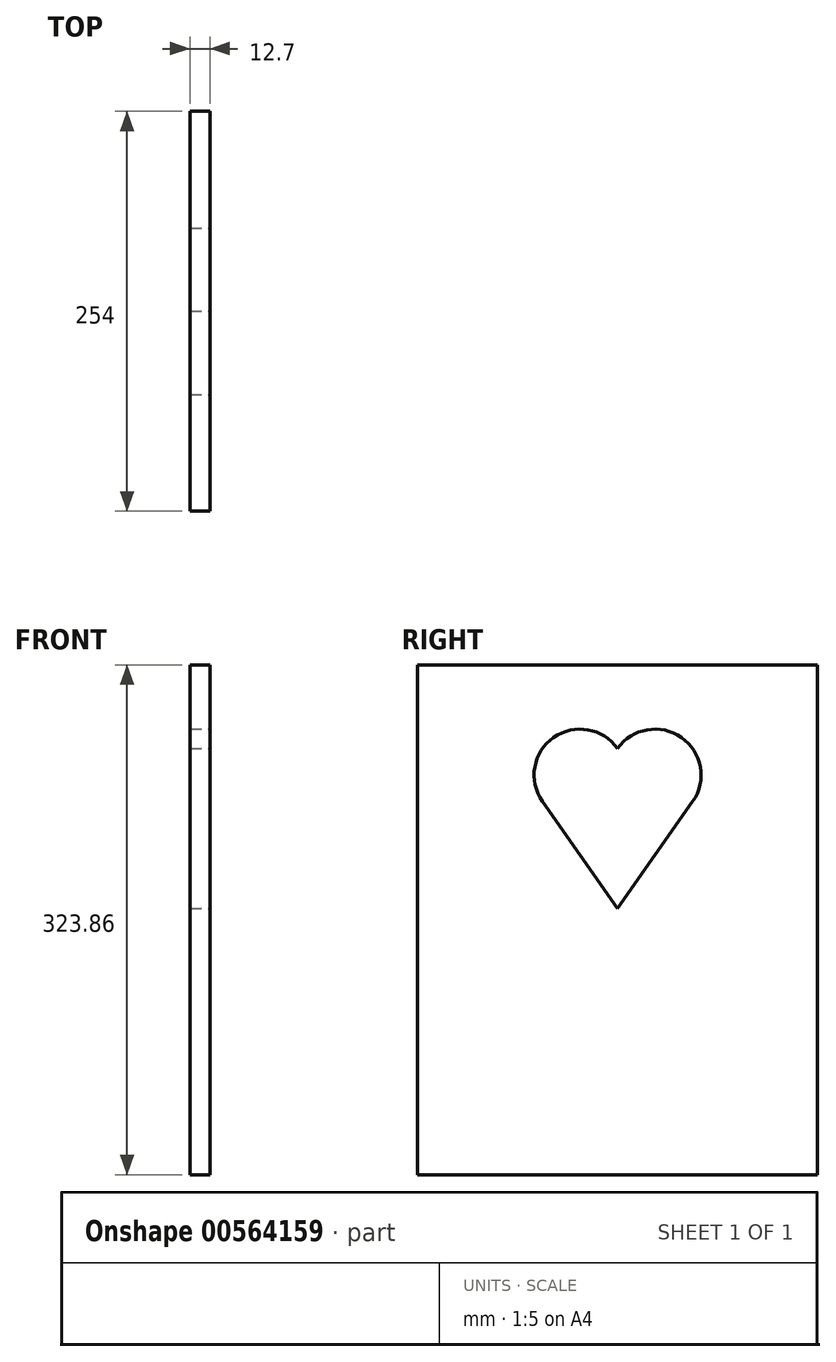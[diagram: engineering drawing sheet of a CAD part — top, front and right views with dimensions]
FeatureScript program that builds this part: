
annotation { "Feature Type Name" : "Feature", "Feature Type Description" : "" }
export const myFeature = defineFeature(function(context is Context, id is Id, definition is map)
    precondition{}
    {
        {
            var Q0;
            Q0=qCreatedBy(makeId("Right.planeOp"),FACE);
            var sketch = newSketch(context, id + "F0", { "sketchPlane" : qUnion([Q0])});
            skLineSegment(sketch, "E0.bottom", {"start": v(-127, 161.93) * mm, "end": v(127, 161.93) * mm});
            skLineSegment(sketch, "E0.top", {"start": v(-127, -161.92) * mm, "end": v(127, -161.92) * mm});
            skLineSegment(sketch, "E0.left", {"start": v(-127, 161.93) * mm, "end": v(-127, -161.92) * mm});
            skLineSegment(sketch, "E0.right", {"start": v(127, 161.93) * mm, "end": v(127, -161.92) * mm});
            skPoint(sketch, "E0.middle", {"position": v(0, 0) * mm});
            skSolve(sketch);
        }
        {
            var Q0;
            Q0=makeQuery(id+"F0.imprint","IMPRINT",FACE,{"disambiguationData":[TD([[makeQuery(id+"F0.imprint","IMPRINT",EDGE,{"derivedFrom":sQuery(id+"F0.wireOp",EDGE,"E0.bottom")}),-1.0]])]});
            extrude(context, id + "F1", {"entities" : qUnion([Q0]), "endBound" : BoundingType.SYMMETRIC, "depth" : 12.7 * mm, "offsetDistance" : 25.4 * mm});
        }
        {
            var Q0;
            Q0=qCreatedBy(makeId("Right.planeOp"),FACE);
            var sketch = newSketch(context, id + "F2", { "sketchPlane" : qUnion([Q0])});
            skLineSegment(sketch, "E1", {"start": v(0, 7.02) * mm, "end": v(47.74, 75.2) * mm});
            skLineSegment(sketch, "E2", {"start": v(47.74, 75.2) * mm, "end": v(0, 75.2) * mm});
            skLineSegment(sketch, "E3", {"start": v(0, 75.2) * mm, "end": v(0, 108.62) * mm});
            skArc(sketch, "E4", {"start": v(47.74, 75.2) * mm, "mid": v(40.58, 115.78) * mm, "end": v(0, 108.62) * mm});
            skPoint(sketch, "E4.third.point", {"position": v(43.6, 70.48) * mm});
            skLineSegment(sketch, "E5", {"start": v(0, 7.02) * mm, "end": v(0, 108.62) * mm});
            skArc(sketch, "E6.MirrorCS", {"start": v(-47.74, 75.2) * mm, "mid": v(-40.58, 115.78) * mm, "end": v(0, 108.62) * mm});
            skLineSegment(sketch, "E7.MirrorCS", {"start": v(0, 7.02) * mm, "end": v(-47.74, 75.2) * mm});
            skSolve(sketch);
        }
        {
            var Q0;
            Q0 = qSketchRegion(id + "F2", true);
            extrude(context, id + "F3", {"entities" : qUnion([Q0]), "operationType" : NewBodyOperationType.REMOVE, "endBound" : BoundingType.SYMMETRIC, "oppositeDirection" : true, "depth" : 25.4 * mm, "offsetDistance" : 25.4 * mm});
        }
    });
